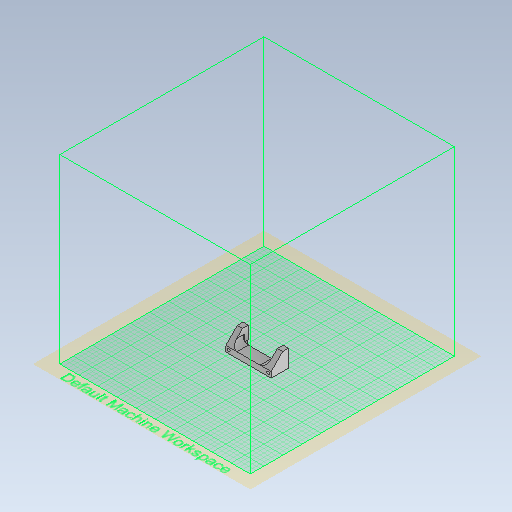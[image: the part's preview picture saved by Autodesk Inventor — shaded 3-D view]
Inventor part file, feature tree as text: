
AUTODESK INVENTOR PART (.ipt)
format: ipt  version: 2021 (Build 250183000, 183)  size: 444,928 bytes
history: native  units: in
note: dims shown in document units (in); Inventor stores cm internally (conversion verified against a paired STEP export)
features: projected_geometry x7, sketch x6, extrude x5, mirror x3, fillet x2, pattern_linear x1, hole x1, chamfer x1
ambient origin geometry x8: Origin, YZ Plane, XZ Plane, XY Plane, X Axis, Y Axis, Z Axis, Center Point
bodies: Solid1 (feature_tree)
feature tree (26):
  extrude  "Extrusion1"  Depth=0.5in
  extrude  "Extrusion2"  Depth=0.46in
  mirror  "Mirror1"
  fillet  "Fillet1"  Radius=0.5in
  extrude  "Extrusion3"  Depth=0.162in
  pattern_linear  "Rectangular Pattern1"  Count1=11 Spacing1=0.25in
  extrude  "Extrusion4"  Depth=0.5in
  mirror  "Mirror2"
  hole  "Hole1"  [1 undecoded]
  mirror  "Mirror3"
  extrude  "Extrusion5"  Depth=0.5in TaperAngle=0.0deg
  chamfer  "Chamfer2"  Distance=0.266in
  fillet  "Fillet3"  Radius=0.276in
  sketch  "Sketch1"  dims[d0=3.938in d1=0.5in]
  sketch  "Sketch2"  dims[d2=1.0in d3=0.0in d4=0.46in d5=0.5in d6=0.0in]
  projected_geometry  "Projected Loop1"
  sketch  "Sketch3"  dims[d7=0.125in d9=0.162in]
  projected_geometry  "Projected Loop2"
  sketch  "Sketch4"  dims[d10=0.087in]
  projected_geometry  "Projected Loop3"
  projected_geometry  "Projected Loop4"
  sketch  "Sketch5"  dims[d11=0.0625in d12=0.0in d13=4.3307in d15=0.25in]
  projected_geometry  "Projected Loop5"
  projected_geometry  "Projected Loop6"
  sketch  "Sketch6"  dims[d19=0.04in d20=0.375in d21=0.02in d22=0.25in d23=0.0in d24=0.266in d25=0.276in d26=0.236in d27=0.194in d28=0.75in d29=0.507in d30=0.25in d31=0.5635in d32=0.12in d33=0.8108in d34=1.0in d35=0.0in d36=1.0in d37=0.125in d38=45.0deg d39=0.5in]
  projected_geometry  "Projected Loop7"
note: 1 required parameter value undecoded (feature->parameter linkage not recoverable at this tier; creation-order binding heuristic only, values carry confidence <= 0.55)
